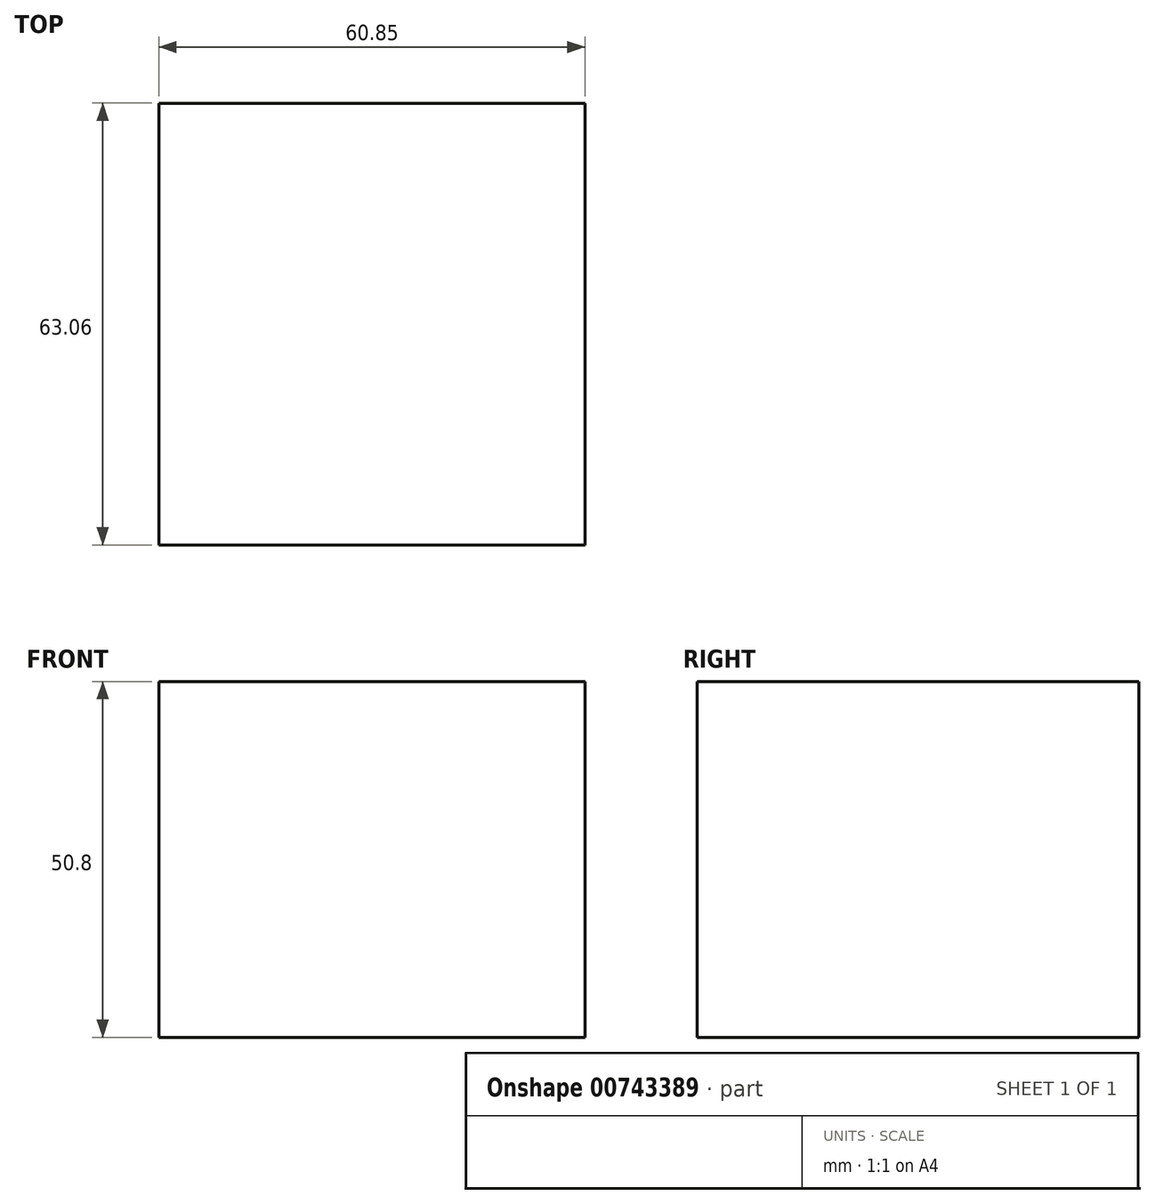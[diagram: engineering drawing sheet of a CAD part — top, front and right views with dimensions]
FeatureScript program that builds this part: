
annotation { "Feature Type Name" : "Feature", "Feature Type Description" : "" }
export const myFeature = defineFeature(function(context is Context, id is Id, definition is map)
    precondition{}
    {
        {
            var Q0;
            Q0=qCreatedBy(makeId("Top.planeOp"),FACE);
            var sketch = newSketch(context, id + "F0", { "sketchPlane" : qUnion([Q0])});
            skLineSegment(sketch, "E0.bottom", {"start": v(-25.49, 40.52) * mm, "end": v(35.36, 40.52) * mm});
            skLineSegment(sketch, "E0.top", {"start": v(-25.49, -22.54) * mm, "end": v(35.36, -22.54) * mm});
            skLineSegment(sketch, "E0.left", {"start": v(-25.49, 40.52) * mm, "end": v(-25.49, -22.54) * mm});
            skLineSegment(sketch, "E0.right", {"start": v(35.36, 40.52) * mm, "end": v(35.36, -22.54) * mm});
            skSolve(sketch);
        }
        {
            var Q0;
            Q0 = qSketchRegion(id + "F0", true);
            extrude(context, id + "F1", {"entities" : qUnion([Q0]), "depth" : 50.8 * mm, "offsetDistance" : 25.4 * mm});
        }
    });
